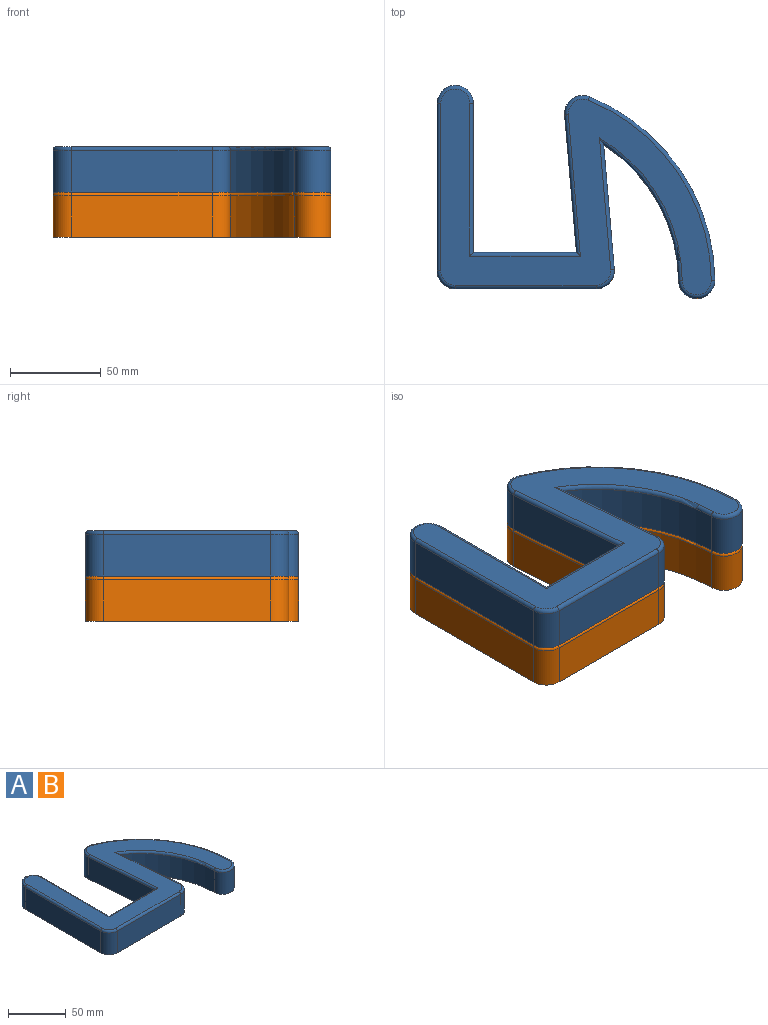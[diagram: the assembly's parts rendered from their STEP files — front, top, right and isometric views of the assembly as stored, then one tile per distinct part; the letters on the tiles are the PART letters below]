
ASSEMBLY  parts=2 mates=1
PART A: 28 faces, bbox 162.9x120.3x25 mm
  f0: plane 92.03x23mm, normal (-1,0,0), area 2116.6mm2, adj f1,f12,f14,f25
  f1: cylinder r=10mm len=23mm, axis (0,0,-1), area 361.3mm2, adj f0,f2,f14,f23
  f2: plane 77.66x23mm, normal (0,-1,0), area 1786.3mm2, adj f1,f3,f14,f21
  f3: cylinder r=10mm len=23mm, axis (0,0,-1), area 381mm2, adj f2,f4,f14,f19
  f4: plane 68.45x23mm, normal (1,0.09,0), area 1580.1mm2, adj f3,f5,f14,f17
  f5: cylinder r=90.18mm len=74.74mm, axis (0,0,-1), area 2045.9mm2, adj f4,f6,f14,f15
  f6: cylinder r=10mm len=23mm, axis (0,0,-1), area 722.6mm2, adj f5,f7,f14,f16
  f7: cylinder r=110.18mm len=100.95mm, axis (0,0,-1), area 2982.7mm2, adj f6,f8,f14,f18
  f8: cylinder r=10mm len=23mm, axis (0,0,-1), area 468.9mm2, adj f7,f9,f14,f20
  f9: plane 75.61x23mm, normal (-1,-0.09,0), area 1745.5mm2, adj f8,f10,f14,f22
  f10: plane 56.77x23mm, normal (0,1,0), area 1305.6mm2, adj f9,f11,f14,f24
  f11: plane 82.03x23mm, normal (1,0,0), area 1886.6mm2, adj f10,f12,f14,f26
  f12: cylinder r=10mm len=23mm, axis (0,0,-1), area 722.6mm2, adj f0,f11,f14,f27
  f13: plane 149.03x113.35mm, normal (0,0,1), area 6117.9mm2, adj f15,f16,f17,f18,f19,f20,f21,f22
  f14: plane 153.03x117.35mm, normal (0,0,-1), area 7685.2mm2, adj f0,f1,f2,f3,f4,f5,f6,f7
  f15: torus R=92.18mm, axis (0,0,1), area 286.3mm2, adj f5,f13,f16,f17
  f16: torus R=8mm, axis (0,0,1), area 91.5mm2, adj f6,f13,f15,f18
  f17: cylinder r=2mm len=72.57mm, axis (0.09,-1,0), area 220.4mm2, adj f4,f13,f15,f19
  f18: torus R=108.18mm, axis (0,0,1), area 404.7mm2, adj f7,f13,f16,f20
  f19: torus R=8mm, axis (0,0,1), area 48.3mm2, adj f3,f13,f17,f21
  f20: torus R=8mm, axis (0,0,1), area 59.4mm2, adj f8,f13,f18,f22
  f21: cylinder r=2mm len=77.66mm, axis (-1,0,0), area 244mm2, adj f2,f13,f19,f23
  f22: cylinder r=2mm len=77.96mm, axis (-0.09,1,0), area 240.9mm2, adj f9,f13,f20,f24
  f23: torus R=8mm, axis (0,0,1), area 45.8mm2, adj f1,f13,f21,f25
  f24: cylinder r=2mm len=60.95mm, axis (1,0,0), area 183.1mm2, adj f10,f13,f22,f26
  f25: cylinder r=2mm len=92.03mm, axis (0,1,0), area 289.1mm2, adj f0,f13,f23,f27
  f26: cylinder r=2mm len=84.03mm, axis (0,-1,0), area 260mm2, adj f11,f13,f24,f27
  f27: torus R=8mm, axis (0,0,1), area 91.5mm2, adj f12,f13,f25,f26
PART B: same geometry as A
PLACE A rot(axis=(1,0,0),0deg) t=(-6.69,6.96,41.23)mm
PLACE B rot(axis=(1,0,0),0deg) t=(-6.69,6.96,16.23)mm
MATE planar A.f1 <-> B.f1  axis (0,0,-1) through (-132.55,-43.77,41.23)mm
